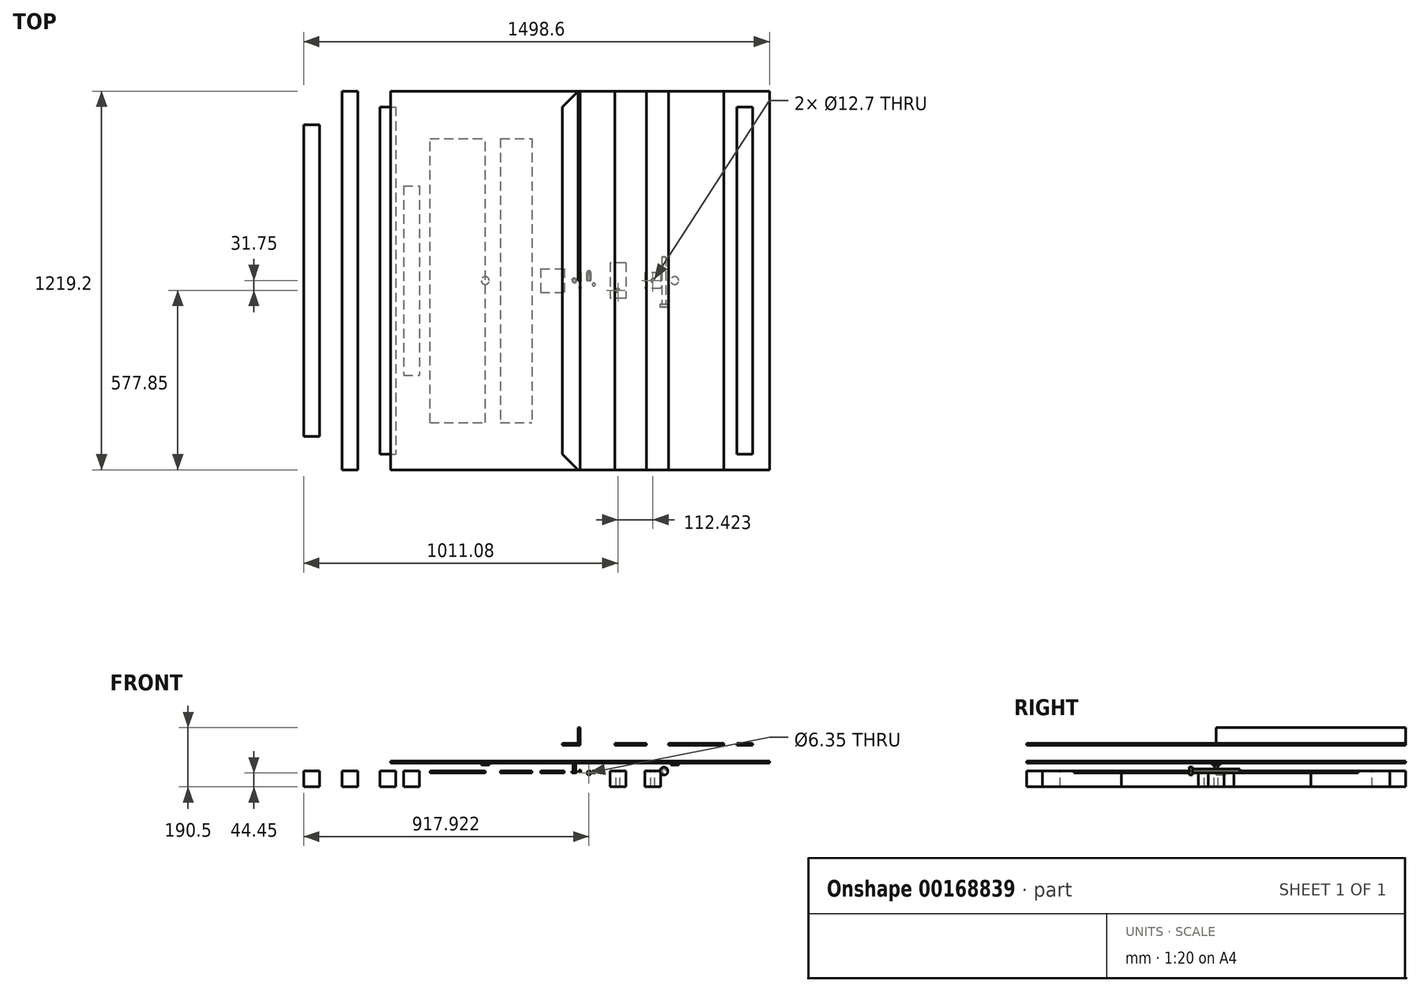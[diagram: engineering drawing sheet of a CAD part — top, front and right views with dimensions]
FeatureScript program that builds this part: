
annotation { "Feature Type Name" : "Feature", "Feature Type Description" : "" }
export const myFeature = defineFeature(function(context is Context, id is Id, definition is map)
    precondition{}
    {
        {
            var Q0;
            Q0=qCreatedBy(makeId("Top.planeOp"),FACE);
            var sketch = newSketch(context, id + "F0", { "sketchPlane" : qUnion([Q0])});
            skLineSegment(sketch, "E0.bottom", {"start": v(-609.6, -609.6) * mm, "end": v(609.6, -609.6) * mm});
            skLineSegment(sketch, "E0.top", {"start": v(-609.6, 609.6) * mm, "end": v(609.6, 609.6) * mm});
            skLineSegment(sketch, "E0.left", {"start": v(-609.6, -609.6) * mm, "end": v(-609.6, 609.6) * mm});
            skLineSegment(sketch, "E0.right", {"start": v(609.6, -609.6) * mm, "end": v(609.6, 609.6) * mm});
            skPoint(sketch, "E0.middle", {"position": v(0, 0) * mm});
            skSolve(sketch);
        }
        {
            var Q0;
            Q0 = qSketchRegion(id + "F0", true);
            extrude(context, id + "F1", {"entities" : qUnion([Q0]), "depth" : 6.35 * mm});
        }
        {
            var Q0;
            Q0=makeQuery(id+"F1.opExtrude","CAP_FACE",FACE,{"disambiguationData":[OSD([sQuery(id+"F0.wireOp",EDGE,"E0.bottom"),sQuery(id+"F0.wireOp",EDGE,"E0.top"),sQuery(id+"F0.wireOp",EDGE,"E0.left"),sQuery(id+"F0.wireOp",EDGE,"E0.right")])],"isStart":true});
            cPlane(context, id + "F2", {"entities" : qUnion([Q0]), "cplaneType" : CPlaneType.OFFSET, "offset" : 25.4 * mm, "width" : 152.4 * mm, "height" : 152.4 * mm});
        }
        {
            var Q0;
            Q0=qCreatedBy(id+"F2.planeOp",FACE);
            var sketch = newSketch(context, id + "F3", { "sketchPlane" : qUnion([Q0])});
            skLineSegment(sketch, "E1", {"start": v(0, 0) * mm, "end": v(0, 488.11) * mm});
            skLineSegment(sketch, "E2.bottom", {"start": v(-482.6, 457.2) * mm, "end": v(-304.8, 457.2) * mm});
            skLineSegment(sketch, "E2.top", {"start": v(-482.6, -457.2) * mm, "end": v(-304.8, -457.2) * mm});
            skLineSegment(sketch, "E2.left", {"start": v(-482.6, 457.2) * mm, "end": v(-482.6, -457.2) * mm});
            skLineSegment(sketch, "E2.right", {"start": v(-304.8, 457.2) * mm, "end": v(-304.8, -457.2) * mm});
            skPoint(sketch, "E2.middle", {"position": v(-393.7, 0) * mm});
            skSolve(sketch);
        }
        {
            var Q0;
            Q0 = qSketchRegion(id + "F3", true);
            extrude(context, id + "F4", {"entities" : qUnion([Q0]), "depth" : 6.35 * mm});
        }
        {
            var Q0;
            Q0=qCreatedBy(id+"F2.planeOp",FACE);
            var sketch = newSketch(context, id + "F5", { "sketchPlane" : qUnion([Q0])});
            skLineSegment(sketch, "E3.bottom", {"start": v(-255.43, -457.2) * mm, "end": v(-153.83, -457.2) * mm});
            skLineSegment(sketch, "E3.top", {"start": v(-255.43, 457.2) * mm, "end": v(-153.83, 457.2) * mm});
            skLineSegment(sketch, "E3.left", {"start": v(-255.43, -457.2) * mm, "end": v(-255.43, 457.2) * mm});
            skLineSegment(sketch, "E3.right", {"start": v(-153.83, -457.2) * mm, "end": v(-153.83, 457.2) * mm});
            skPoint(sketch, "E3.middle", {"position": v(-204.63, 0) * mm});
            skSolve(sketch);
        }
        {
            var Q0;
            Q0 = qSketchRegion(id + "F5", true);
            extrude(context, id + "F6", {"entities" : qUnion([Q0]), "depth" : 6.35 * mm});
        }
        {
            var Q0;
            Q0=makeQuery(id+"F1.opExtrude","CAP_FACE",FACE,{"disambiguationData":[OSD([sQuery(id+"F0.wireOp",EDGE,"E0.bottom"),sQuery(id+"F0.wireOp",EDGE,"E0.top"),sQuery(id+"F0.wireOp",EDGE,"E0.left"),sQuery(id+"F0.wireOp",EDGE,"E0.right")])],"isStart":true});
            var sketch = newSketch(context, id + "F7", { "sketchPlane" : qUnion([Q0])});
            skLineSegment(sketch, "E4", {"start": v(0, 0) * mm, "end": v(304.8, 0) * mm});
            skLineSegment(sketch, "E5", {"start": v(0, 0) * mm, "end": v(-304.8, 0) * mm});
            skCircle(sketch, "E6", {"center": v(304.8, 0) * mm, "radius": 12.7 * mm});
            skLineSegment(sketch, "E7", {"start": v(0, 0) * mm, "end": v(0, 9.59) * mm});
            skCircle(sketch, "E8.MirrorC", {"center": v(-304.8, 0) * mm, "radius": 12.7 * mm});
            skSolve(sketch);
        }
        {
            var Q0;
            Q0 = qSketchRegion(id + "F7", true);
            extrude(context, id + "F8", {"entities" : qUnion([Q0]), "operationType" : NewBodyOperationType.ADD, "depth" : 6.35 * mm});
        }
        {
            var Q0;
            Q0=qCreatedBy(id+"F2.planeOp",FACE);
            var sketch = newSketch(context, id + "F9", { "sketchPlane" : qUnion([Q0])});
            skLineSegment(sketch, "E9.bottom", {"start": v(-567.66, -304.8) * mm, "end": v(-516.86, -304.8) * mm});
            skLineSegment(sketch, "E9.top", {"start": v(-567.66, 304.8) * mm, "end": v(-516.86, 304.8) * mm});
            skLineSegment(sketch, "E9.left", {"start": v(-567.66, -304.8) * mm, "end": v(-567.66, 304.8) * mm});
            skLineSegment(sketch, "E9.right", {"start": v(-516.86, -304.8) * mm, "end": v(-516.86, 304.8) * mm});
            skPoint(sketch, "E9.middle", {"position": v(-542.26, 0) * mm});
            skSolve(sketch);
        }
        {
            var Q0;
            Q0 = qSketchRegion(id + "F9", true);
            extrude(context, id + "F10", {"entities" : qUnion([Q0]), "depth" : 50.8 * mm});
        }
        {
            var Q0;
            Q0=qCreatedBy(id+"F2.planeOp",FACE);
            var sketch = newSketch(context, id + "F11", { "sketchPlane" : qUnion([Q0])});
            skLineSegment(sketch, "E10.bottom", {"start": v(-764.89, -609.6) * mm, "end": v(-714.09, -609.6) * mm});
            skLineSegment(sketch, "E10.top", {"start": v(-764.89, 609.6) * mm, "end": v(-714.09, 609.6) * mm});
            skLineSegment(sketch, "E10.left", {"start": v(-764.89, -609.6) * mm, "end": v(-764.89, 609.6) * mm});
            skLineSegment(sketch, "E10.right", {"start": v(-714.09, -609.6) * mm, "end": v(-714.09, 609.6) * mm});
            skPoint(sketch, "E10.middle", {"position": v(-739.49, 0) * mm});
            skSolve(sketch);
        }
        {
            var Q0;
            Q0 = qSketchRegion(id + "F11", true);
            extrude(context, id + "F12", {"entities" : qUnion([Q0]), "depth" : 50.8 * mm});
        }
        {
            var Q0;
            Q0=qCreatedBy(id+"F2.planeOp",FACE);
            var sketch = newSketch(context, id + "F13", { "sketchPlane" : qUnion([Q0])});
            skLineSegment(sketch, "E11.bottom", {"start": v(-643.3, -558.8) * mm, "end": v(-592.5, -558.8) * mm});
            skLineSegment(sketch, "E11.top", {"start": v(-643.3, 558.8) * mm, "end": v(-592.5, 558.8) * mm});
            skLineSegment(sketch, "E11.left", {"start": v(-643.3, -558.8) * mm, "end": v(-643.3, 558.8) * mm});
            skLineSegment(sketch, "E11.right", {"start": v(-592.5, -558.8) * mm, "end": v(-592.5, 558.8) * mm});
            skPoint(sketch, "E11.middle", {"position": v(-617.9, 0) * mm});
            skSolve(sketch);
        }
        {
            var Q0;
            Q0 = qSketchRegion(id + "F13", true);
            extrude(context, id + "F14", {"entities" : qUnion([Q0]), "depth" : 50.8 * mm});
        }
        {
            var Q0;
            Q0=qCreatedBy(id+"F2.planeOp",FACE);
            var sketch = newSketch(context, id + "F15", { "sketchPlane" : qUnion([Q0])});
            skLineSegment(sketch, "E12.bottom", {"start": v(54.32, -25.4) * mm, "end": v(28.92, -25.4) * mm});
            skLineSegment(sketch, "E12.top", {"start": v(54.32, 25.4) * mm, "end": v(28.92, 25.4) * mm});
            skLineSegment(sketch, "E12.left", {"start": v(54.32, -25.4) * mm, "end": v(54.32, 25.4) * mm});
            skLineSegment(sketch, "E12.right", {"start": v(28.92, -25.4) * mm, "end": v(28.92, 25.4) * mm});
            skPoint(sketch, "E12.middle", {"position": v(41.62, 0) * mm});
            skSolve(sketch);
        }
        {
            var Q0;
            Q0 = qSketchRegion(id + "F15", true);
            extrude(context, id + "F16", {"entities" : qUnion([Q0]), "depth" : 6.35 * mm});
        }
        {
            var Q0;
            Q0=makeQuery(id+"F16.opExtrude","SWEPT_FACE",FACE,{"disambiguationData":[OSD([sQuery(id+"F15.wireOp",EDGE,"E12.bottom")])]});
            var sketch = newSketch(context, id + "F17", { "sketchPlane" : qUnion([Q0])});
            skCircle(sketch, "E13", {"center": v(-28.92, -31.75) * mm, "radius": 6.35 * mm});
            skCircle(sketch, "E14", {"center": v(-28.92, -31.75) * mm, "radius": 3.18 * mm});
            skLineSegment(sketch, "E15", {"start": v(-28.92, -31.75) * mm, "end": v(-28.92, -38.1) * mm});
            skLineSegment(sketch, "E16", {"start": v(-28.92, -38.1) * mm, "end": v(-28.92, -25.4) * mm});
            skSolve(sketch);
        }
        {
            var Q0;
            Q0 = qSketchRegion(id + "F17", true);
            extrude(context, id + "F18", {"entities" : qUnion([Q0]), "operationType" : NewBodyOperationType.ADD, "oppositeDirection" : true, "depth" : 25.4 * mm});
        }
        {
            var Q0;
            {var subQ0=sQuery(id+"F17.wireOp",EDGE,"E16");var subQ1=sQuery(id+"F17.wireOp",EDGE,"E14");var subQ2=makeQuery(id+"F17.imprint","INTERSECT",VERTEX,{"disambiguationData":[OD(0.0)],"derivedFrom":[subQ1,subQ0]});Q0=makeQuery(id+"F17.imprint","IMPRINT",FACE,{"disambiguationData":[TD([[makeQuery(id+"F17.imprint","IMPRINT",EDGE,{"disambiguationData":[TD([[subQ2,1.0]])],"derivedFrom":subQ1}),1.0]])]});}
            var Q1;
            {var subQ0=sQuery(id+"F17.wireOp",EDGE,"E16");var subQ1=sQuery(id+"F17.wireOp",EDGE,"E14");var subQ2=makeQuery(id+"F17.imprint","INTERSECT",VERTEX,{"disambiguationData":[OD(1.0)],"derivedFrom":[subQ1,subQ0]});Q1=makeQuery(id+"F17.imprint","IMPRINT",FACE,{"disambiguationData":[TD([[makeQuery(id+"F17.imprint","IMPRINT",EDGE,{"disambiguationData":[TD([[subQ2,1.0]])],"derivedFrom":subQ1}),1.0]])]});}
            var Q2;
            {var subQ0=sQuery(id+"F17.wireOp",EDGE,"E16");var subQ1=sQuery(id+"F17.wireOp",EDGE,"E14");var subQ2=makeQuery(id+"F17.imprint","INTERSECT",VERTEX,{"disambiguationData":[OD(0.0)],"derivedFrom":[subQ1,subQ0]});Q2=makeQuery(id+"F17.imprint","IMPRINT",FACE,{"disambiguationData":[TD([[makeQuery(id+"F17.imprint","IMPRINT",EDGE,{"disambiguationData":[TD([[subQ2,-1.0]])],"derivedFrom":subQ1}),1.0]])]});}
            extrude(context, id + "F19", {"entities" : qUnion([Q0, Q1, Q2]), "operationType" : NewBodyOperationType.REMOVE, "oppositeDirection" : true, "depth" : 50.8 * mm});
        }
        {
            var Q0;
            {var subQ0=sQuery(id+"F17.wireOp",EDGE,"E16");var subQ4=sQuery(id+"F17.wireOp",EDGE,"E14");var subQ6=makeQuery(id+"F17.imprint","INTERSECT",VERTEX,{"disambiguationData":[OD(0.0)],"derivedFrom":[subQ4,subQ0]});Q0=makeQuery(id+"F17.imprint","IMPRINT",FACE,{"disambiguationData":[TD([[makeQuery(id+"F17.imprint","IMPRINT",EDGE,{"disambiguationData":[TD([[subQ6,1.0]])],"derivedFrom":subQ4}),-1.0]])]});}
            var Q1;
            Q1=sQuery(id+"F17.wireOp",EDGE,"E16");
            revolve(context, id + "F20", {"operationType" : NewBodyOperationType.ADD, "entities" : qUnion([Q0]), "axis" : qUnion([Q1]), "revolveType" : RevolveType.FULL});
        }
        {
            var Q0;
            Q0=makeQuery(id+"F16.opExtrude","SWEPT_FACE",FACE,{"disambiguationData":[OSD([sQuery(id+"F15.wireOp",EDGE,"E12.top")])]});
            var sketch = newSketch(context, id + "F21", { "sketchPlane" : qUnion([Q0])});
            skLineSegment(sketch, "E17", {"start": v(31.97, -31.75) * mm, "end": v(35.27, -31.75) * mm});
            skLineSegment(sketch, "E18", {"start": v(35.27, -31.75) * mm, "end": v(35.27, -25.4) * mm});
            skLineSegment(sketch, "E19", {"start": v(35.27, -25.4) * mm, "end": v(28.92, -25.4) * mm});
            skLineSegment(sketch, "E20", {"start": v(31.97, -31.75) * mm, "end": v(28.92, -31.75) * mm});
            skLineSegment(sketch, "E21", {"start": v(28.92, -31.75) * mm, "end": v(28.92, -25.4) * mm});
            skSolve(sketch);
        }
        {
            var Q0;
            Q0 = qSketchRegion(id + "F21", true);
            extrude(context, id + "F22", {"entities" : qUnion([Q0]), "operationType" : NewBodyOperationType.REMOVE, "oppositeDirection" : true, "depth" : 25.4 * mm});
        }
        {
            var Q0;
            Q0=makeQuery(id+"F16.opExtrude","CAP_FACE",FACE,{"disambiguationData":[OSD([sQuery(id+"F15.wireOp",EDGE,"E12.bottom"),sQuery(id+"F15.wireOp",EDGE,"E12.top"),sQuery(id+"F15.wireOp",EDGE,"E12.left"),sQuery(id+"F15.wireOp",EDGE,"E12.right")])],"isStart":false});
            var sketch = newSketch(context, id + "F23", { "sketchPlane" : qUnion([Q0])});
            skLineSegment(sketch, "E22", {"start": v(44.8, -25.4) * mm, "end": v(44.8, -19.05) * mm});
            skLineSegment(sketch, "E23", {"start": v(44.8, -19.05) * mm, "end": v(44.8, -12.7) * mm});
            skCircle(sketch, "E24", {"center": v(44.8, -12.7) * mm, "radius": 4.76 * mm});
            skLineSegment(sketch, "E25", {"start": v(54.32, 0) * mm, "end": v(49.81, 0) * mm});
            skPoint(sketch, "E25.endSnap0", {"position": v(54.32, 0) * mm});
            skCircle(sketch, "E26.MirrorC", {"center": v(44.8, 12.7) * mm, "radius": 4.76 * mm});
            skSolve(sketch);
        }
        {
            var Q0;
            Q0=makeQuery(id+"F23.imprint","IMPRINT",FACE,{"disambiguationData":[TD([[makeQuery(id+"F23.imprint","IMPRINT",EDGE,{"derivedFrom":sQuery(id+"F23.wireOp",EDGE,"E26.MirrorC")}),-1.0]])]});
            var Q1;
            Q1=makeQuery(id+"F23.imprint","IMPRINT",FACE,{"disambiguationData":[TD([[makeQuery(id+"F23.imprint","IMPRINT",EDGE,{"derivedFrom":sQuery(id+"F23.wireOp",EDGE,"E24")}),1.0]])]});
            extrude(context, id + "F24", {"entities" : qUnion([Q0, Q1]), "operationType" : NewBodyOperationType.REMOVE, "oppositeDirection" : true, "depth" : 25.4 * mm});
        }
        {
            var Q0;
            Q0=qCreatedBy(id+"F2.planeOp",FACE);
            var sketch = newSketch(context, id + "F25", { "sketchPlane" : qUnion([Q0])});
            skLineSegment(sketch, "E27.bottom", {"start": v(3.17, -25.4) * mm, "end": v(-3.18, -25.4) * mm});
            skLineSegment(sketch, "E27.top", {"start": v(3.18, 25.4) * mm, "end": v(-3.17, 25.4) * mm});
            skLineSegment(sketch, "E27.left", {"start": v(3.17, -25.4) * mm, "end": v(3.18, 25.4) * mm});
            skLineSegment(sketch, "E27.right", {"start": v(-3.18, -25.4) * mm, "end": v(-3.17, 25.4) * mm});
            skPoint(sketch, "E27.middle", {"position": v(0, 0) * mm});
            skLineSegment(sketch, "E28", {"start": v(0, 25.4) * mm, "end": v(0, -25.4) * mm});
            skCircle(sketch, "E29.cCircle", {"center": v(-18.15, 0) * mm, "radius": 7.14 * mm, "construction": true});
            skLineSegment(sketch, "E29.0", {"start": v(-11.25, -4.52) * mm, "end": v(-18.61, -8.24) * mm});
            skLineSegment(sketch, "E29.1", {"start": v(-18.61, -8.24) * mm, "end": v(-25.51, -3.72) * mm});
            skLineSegment(sketch, "E29.2", {"start": v(-25.51, -3.72) * mm, "end": v(-25.05, 4.52) * mm});
            skLineSegment(sketch, "E29.3", {"start": v(-25.05, 4.52) * mm, "end": v(-17.69, 8.24) * mm});
            skLineSegment(sketch, "E29.4", {"start": v(-17.69, 8.24) * mm, "end": v(-10.78, 3.72) * mm});
            skLineSegment(sketch, "E29.5", {"start": v(-10.78, 3.72) * mm, "end": v(-11.25, -4.52) * mm});
            skPoint(sketch, "E29.0.midPoint", {"position": v(-14.93, -6.38) * mm});
            skCircle(sketch, "E30", {"center": v(-18.15, 0) * mm, "radius": 4.76 * mm});
            skSolve(sketch);
        }
        {
            var Q0;
            {var subQ0=sQuery(id+"F25.wireOp",EDGE,"E27.right");Q0=makeQuery(id+"F25.imprint","IMPRINT",FACE,{"disambiguationData":[TD([[makeQuery(id+"F25.imprint","IMPRINT",EDGE,{"derivedFrom":subQ0}),-1.0]])]});}
            var Q1;
            Q1=sQuery(id+"F25.wireOp",EDGE,"E28");
            revolve(context, id + "F26", {"entities" : qUnion([Q0]), "axis" : qUnion([Q1]), "revolveType" : RevolveType.FULL});
        }
        {
            var Q0;
            Q0=makeQuery(id+"F25.imprint","IMPRINT",FACE,{"disambiguationData":[TD([[makeQuery(id+"F25.imprint","IMPRINT",EDGE,{"derivedFrom":sQuery(id+"F25.wireOp",EDGE,"E30")}),1.0]])]});
            extrude(context, id + "F27", {"entities" : qUnion([Q0]), "oppositeDirection" : true, "depth" : 25.4 * mm});
        }
        {
            var Q0;
            Q0=makeQuery(id+"F25.imprint","IMPRINT",FACE,{"disambiguationData":[TD([[makeQuery(id+"F25.imprint","IMPRINT",EDGE,{"derivedFrom":sQuery(id+"F25.wireOp",EDGE,"E29.0")}),-1.0]])]});
            var Q1;
            Q1=makeQuery(id+"F25.imprint","IMPRINT",FACE,{"disambiguationData":[TD([[makeQuery(id+"F25.imprint","IMPRINT",EDGE,{"derivedFrom":sQuery(id+"F25.wireOp",EDGE,"E30")}),1.0]])]});
            extrude(context, id + "F28", {"entities" : qUnion([Q0, Q1]), "operationType" : NewBodyOperationType.ADD, "depth" : 6.35 * mm});
        }
        {
            var Q0;
            Q0=qCreatedBy(id+"F2.planeOp",FACE);
            var sketch = newSketch(context, id + "F29", { "sketchPlane" : qUnion([Q0])});
            skLineSegment(sketch, "E31.bottom", {"start": v(-889, -501.65) * mm, "end": v(-838.2, -501.65) * mm});
            skLineSegment(sketch, "E31.top", {"start": v(-889, 501.65) * mm, "end": v(-838.2, 501.65) * mm});
            skLineSegment(sketch, "E31.left", {"start": v(-889, -501.65) * mm, "end": v(-889, 501.65) * mm});
            skLineSegment(sketch, "E31.right", {"start": v(-838.2, -501.65) * mm, "end": v(-838.2, 501.65) * mm});
            skPoint(sketch, "E31.middle", {"position": v(-863.6, 0) * mm});
            skLineSegment(sketch, "E32", {"start": v(-863.6, 0) * mm, "end": v(0, 0) * mm});
            skSolve(sketch);
        }
        {
            var Q0;
            {var subQ0=sQuery(id+"F29.wireOp",EDGE,"E31.bottom");Q0=makeQuery(id+"F29.imprint","IMPRINT",FACE,{"disambiguationData":[TD([[makeQuery(id+"F29.imprint","IMPRINT",EDGE,{"derivedFrom":subQ0}),1.0]])]});}
            extrude(context, id + "F30", {"entities" : qUnion([Q0]), "depth" : 50.8 * mm});
        }
        {
            var Q0;
            Q0=qCreatedBy(id+"F2.planeOp",FACE);
            var sketch = newSketch(context, id + "F31", { "sketchPlane" : qUnion([Q0])});
            skLineSegment(sketch, "E33.bottom", {"start": v(-127, -38.1) * mm, "end": v(-50.8, -38.1) * mm});
            skLineSegment(sketch, "E33.top", {"start": v(-127, 38.1) * mm, "end": v(-50.8, 38.1) * mm});
            skLineSegment(sketch, "E33.left", {"start": v(-127, -38.1) * mm, "end": v(-127, 38.1) * mm});
            skLineSegment(sketch, "E33.right", {"start": v(-50.8, -38.1) * mm, "end": v(-50.8, 38.1) * mm});
            skPoint(sketch, "E33.middle", {"position": v(-88.9, 0) * mm});
            skLineSegment(sketch, "E34", {"start": v(0, 0) * mm, "end": v(-50.8, 0) * mm});
            skSolve(sketch);
        }
        {
            var Q0;
            Q0 = qSketchRegion(id + "F31", true);
            extrude(context, id + "F32", {"entities" : qUnion([Q0]), "depth" : 6.35 * mm});
        }
        {
            var Q0;
            Q0=qCreatedBy(id+"F2.planeOp",FACE);
            var sketch = newSketch(context, id + "F33", { "sketchPlane" : qUnion([Q0])});
            skLineSegment(sketch, "E35.bottom", {"start": v(147.48, -57.15) * mm, "end": v(96.68, -57.15) * mm});
            skLineSegment(sketch, "E35.top", {"start": v(147.48, 57.15) * mm, "end": v(96.68, 57.15) * mm});
            skLineSegment(sketch, "E35.left", {"start": v(147.48, -57.15) * mm, "end": v(147.48, 57.15) * mm});
            skLineSegment(sketch, "E35.right", {"start": v(96.68, -57.15) * mm, "end": v(96.68, 57.15) * mm});
            skPoint(sketch, "E35.middle", {"position": v(122.08, 0) * mm});
            skLineSegment(sketch, "E36", {"start": v(122.08, 57.15) * mm, "end": v(122.08, 31.75) * mm});
            skCircle(sketch, "E37", {"center": v(122.08, 31.75) * mm, "radius": 6.35 * mm});
            skSolve(sketch);
        }
        {
            var Q0;
            Q0 = qSketchRegion(id + "F33", true);
            extrude(context, id + "F34", {"entities" : qUnion([Q0]), "depth" : 50.8 * mm});
        }
        {
            var Q0;
            Q0=qCreatedBy(id+"F2.planeOp",FACE);
            var sketch = newSketch(context, id + "F35", { "sketchPlane" : qUnion([Q0])});
            skLineSegment(sketch, "E38.bottom", {"start": v(259.9, -25.4) * mm, "end": v(209.1, -25.4) * mm});
            skLineSegment(sketch, "E38.top", {"start": v(259.9, 25.4) * mm, "end": v(209.1, 25.4) * mm});
            skLineSegment(sketch, "E38.left", {"start": v(259.9, -25.4) * mm, "end": v(259.9, 25.4) * mm});
            skLineSegment(sketch, "E38.right", {"start": v(209.1, -25.4) * mm, "end": v(209.1, 25.4) * mm});
            skPoint(sketch, "E38.middle", {"position": v(234.5, 0) * mm});
            skLineSegment(sketch, "E39", {"start": v(234.5, 25.4) * mm, "end": v(234.5, 0) * mm});
            skPoint(sketch, "E39.endSnap0", {"position": v(234.5, 25.4) * mm});
            skCircle(sketch, "E40", {"center": v(234.5, 0) * mm, "radius": 6.35 * mm});
            skLineSegment(sketch, "E41.bottom", {"start": v(276.65, -76.2) * mm, "end": v(263.95, -76.2) * mm});
            skLineSegment(sketch, "E41.top", {"start": v(276.65, 76.2) * mm, "end": v(263.95, 76.2) * mm});
            skLineSegment(sketch, "E41.left", {"start": v(276.65, -76.2) * mm, "end": v(276.65, 76.2) * mm});
            skLineSegment(sketch, "E41.right", {"start": v(263.95, -76.2) * mm, "end": v(263.95, 76.2) * mm});
            skPoint(sketch, "E41.middle", {"position": v(270.3, 0) * mm});
            skLineSegment(sketch, "E42.bottom", {"start": v(283, 76.2) * mm, "end": v(257.6, 76.2) * mm});
            skLineSegment(sketch, "E42.top", {"start": v(283, 76.2) * mm, "end": v(257.6, 76.2) * mm});
            skLineSegment(sketch, "E42.left", {"start": v(283, 76.2) * mm, "end": v(283, 76.2) * mm});
            skLineSegment(sketch, "E42.right", {"start": v(257.6, 76.2) * mm, "end": v(257.6, 76.2) * mm});
            skPoint(sketch, "E42.middle", {"position": v(270.3, 76.2) * mm});
            skPoint(sketch, "E42.cornerSnap0", {"position": v(270.3, 76.2) * mm});
            skLineSegment(sketch, "E43", {"start": v(257.6, 76.2) * mm, "end": v(257.6, 85.86) * mm});
            skLineSegment(sketch, "E44", {"start": v(257.6, 85.86) * mm, "end": v(283, 85.86) * mm});
            skLineSegment(sketch, "E45", {"start": v(270.3, 76.2) * mm, "end": v(270.3, 85.86) * mm});
            skLineSegment(sketch, "E46.MirrorCS", {"start": v(283, 76.2) * mm, "end": v(283, 85.86) * mm});
            skLineSegment(sketch, "E47", {"start": v(270.3, 76.2) * mm, "end": v(270.3, -76.2) * mm});
            skSolve(sketch);
        }
        {
            var Q0;
            Q0=makeQuery(id+"F35.imprint","IMPRINT",FACE,{"disambiguationData":[TD([[makeQuery(id+"F35.imprint","IMPRINT",EDGE,{"derivedFrom":sQuery(id+"F35.wireOp",EDGE,"E38.bottom")}),-1.0]])]});
            extrude(context, id + "F36", {"entities" : qUnion([Q0]), "depth" : 50.8 * mm});
        }
        {
            var Q0;
            {var subQ0=sQuery(id+"F35.wireOp",EDGE,"E41.left");Q0=makeQuery(id+"F35.imprint","IMPRINT",FACE,{"disambiguationData":[TD([[makeQuery(id+"F35.imprint","IMPRINT",EDGE,{"derivedFrom":subQ0}),1.0]])]});}
            var Q1;
            {var subQ0=sQuery(id+"F35.wireOp",EDGE,"E45");Q1=makeQuery(id+"F35.imprint","IMPRINT",FACE,{"disambiguationData":[TD([[makeQuery(id+"F35.imprint","IMPRINT",EDGE,{"derivedFrom":subQ0}),-1.0]])]});}
            var Q2;
            Q2=sQuery(id+"F35.wireOp",EDGE,"E47");
            revolve(context, id + "F37", {"entities" : qUnion([Q0, Q1]), "axis" : qUnion([Q2]), "revolveType" : RevolveType.FULL});
        }
        {
            var Q0;
            Q0=makeQuery(id+"F1.opExtrude","CAP_FACE",FACE,{"disambiguationData":[OSD([sQuery(id+"F0.wireOp",EDGE,"E0.bottom"),sQuery(id+"F0.wireOp",EDGE,"E0.top"),sQuery(id+"F0.wireOp",EDGE,"E0.left"),sQuery(id+"F0.wireOp",EDGE,"E0.right")])],"isStart":false});
            cPlane(context, id + "F38", {"entities" : qUnion([Q0]), "cplaneType" : CPlaneType.OFFSET, "offset" : 50.8 * mm, "width" : 152.4 * mm, "height" : 152.4 * mm});
        }
        {
            var Q0;
            Q0=qCreatedBy(id+"F38.planeOp",FACE);
            var sketch = newSketch(context, id + "F39", { "sketchPlane" : qUnion([Q0])});
            skLineSegment(sketch, "E48", {"start": v(0, 0) * mm, "end": v(0, 609.6) * mm});
            skLineSegment(sketch, "E49", {"start": v(0, 0) * mm, "end": v(-57.15, 0) * mm});
            skLineSegment(sketch, "E50", {"start": v(-57.15, 0) * mm, "end": v(-57.15, 558.8) * mm});
            skLineSegment(sketch, "E51", {"start": v(0, 609.6) * mm, "end": v(-6.35, 609.6) * mm});
            skLineSegment(sketch, "E52", {"start": v(-6.35, 609.6) * mm, "end": v(-57.15, 558.8) * mm});
            skLineSegment(sketch, "E53", {"start": v(-6.35, 609.6) * mm, "end": v(-6.35, 0) * mm});
            skLineSegment(sketch, "E54", {"start": v(0, 0) * mm, "end": v(-6.35, 0) * mm});
            skLineSegment(sketch, "E55.MirrorCS", {"start": v(0, 0) * mm, "end": v(0, -609.6) * mm});
            skLineSegment(sketch, "E56.MirrorCS", {"start": v(-6.35, -609.6) * mm, "end": v(-6.35, 0) * mm});
            skLineSegment(sketch, "E57.MirrorCS", {"start": v(-57.15, 0) * mm, "end": v(-57.15, -558.8) * mm});
            skLineSegment(sketch, "E58.MirrorCS", {"start": v(-6.35, -609.6) * mm, "end": v(-57.15, -558.8) * mm});
            skLineSegment(sketch, "E59.MirrorCS", {"start": v(0, -609.6) * mm, "end": v(-6.35, -609.6) * mm});
            skSolve(sketch);
        }
        {
            var Q0;
            Q0 = qSketchRegion(id + "F39", true);
            extrude(context, id + "F40", {"entities" : qUnion([Q0]), "depth" : 6.35 * mm});
        }
        {
            var Q0;
            Q0=makeQuery(id+"F39.imprint","IMPRINT",FACE,{"disambiguationData":[TD([[makeQuery(id+"F39.imprint","IMPRINT",EDGE,{"derivedFrom":sQuery(id+"F39.wireOp",EDGE,"E48")}),1.0]])]});
            var Q1;
            Q1=makeQuery(id+"F39.imprint","IMPRINT",FACE,{"disambiguationData":[TD([[makeQuery(id+"F39.imprint","IMPRINT",EDGE,{"derivedFrom":sQuery(id+"F39.wireOp",EDGE,"E54")}),1.0]])]});
            extrude(context, id + "F41", {"entities" : qUnion([Q0, Q1]), "depth" : 57.15 * mm});
        }
        {
            var Q0;
            Q0=qCreatedBy(id+"F38.planeOp",FACE);
            var sketch = newSketch(context, id + "F42", { "sketchPlane" : qUnion([Q0])});
            skLineSegment(sketch, "E60.bottom", {"start": v(462.47, -609.6) * mm, "end": v(284.67, -609.6) * mm});
            skLineSegment(sketch, "E60.top", {"start": v(462.47, 609.6) * mm, "end": v(284.67, 609.6) * mm});
            skLineSegment(sketch, "E60.left", {"start": v(462.47, -609.6) * mm, "end": v(462.47, 609.6) * mm});
            skLineSegment(sketch, "E60.right", {"start": v(284.67, -609.6) * mm, "end": v(284.67, 609.6) * mm});
            skPoint(sketch, "E60.middle", {"position": v(373.57, 0) * mm});
            skLineSegment(sketch, "E61.bottom", {"start": v(214.18, -609.6) * mm, "end": v(112.58, -609.6) * mm});
            skLineSegment(sketch, "E61.top", {"start": v(214.18, 609.6) * mm, "end": v(112.58, 609.6) * mm});
            skLineSegment(sketch, "E61.left", {"start": v(214.18, -609.6) * mm, "end": v(214.18, 609.6) * mm});
            skLineSegment(sketch, "E61.right", {"start": v(112.58, -609.6) * mm, "end": v(112.58, 609.6) * mm});
            skPoint(sketch, "E61.middle", {"position": v(163.38, 0) * mm});
            skLineSegment(sketch, "E62.bottom", {"start": v(556.15, -558.8) * mm, "end": v(505.35, -558.8) * mm});
            skLineSegment(sketch, "E62.top", {"start": v(556.15, 558.8) * mm, "end": v(505.35, 558.8) * mm});
            skLineSegment(sketch, "E62.left", {"start": v(556.15, -558.8) * mm, "end": v(556.15, 558.8) * mm});
            skLineSegment(sketch, "E62.right", {"start": v(505.35, -558.8) * mm, "end": v(505.35, 558.8) * mm});
            skPoint(sketch, "E62.middle", {"position": v(530.75, 0) * mm});
            skSolve(sketch);
        }
        {
            var Q0;
            Q0 = qSketchRegion(id + "F42", true);
            extrude(context, id + "F43", {"entities" : qUnion([Q0]), "depth" : 6.35 * mm});
        }
    });
